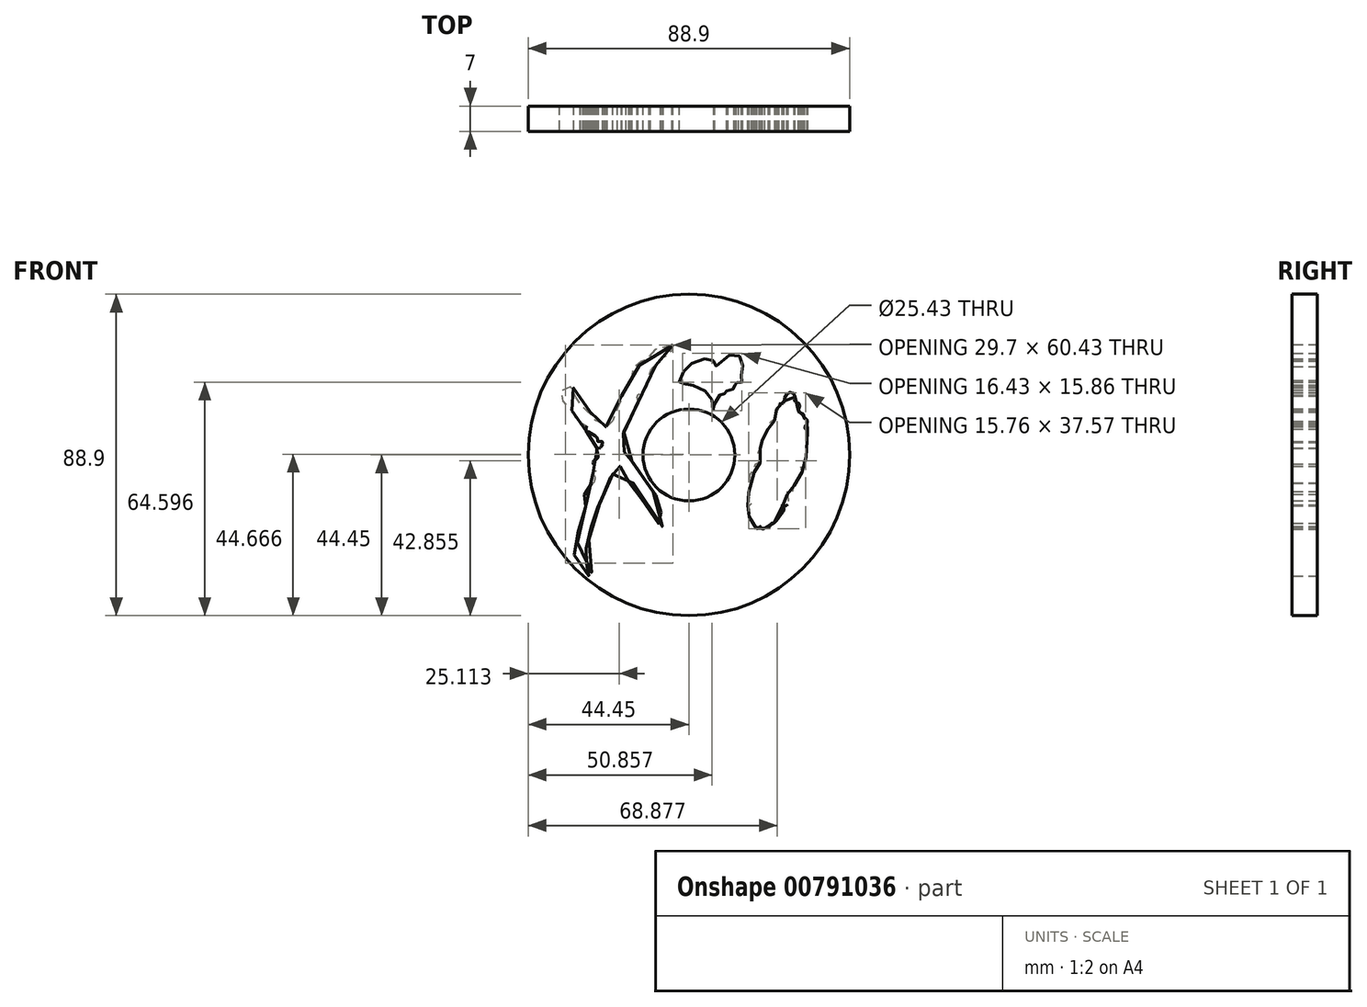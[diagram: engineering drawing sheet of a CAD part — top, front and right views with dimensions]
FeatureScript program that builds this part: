
annotation { "Feature Type Name" : "Feature", "Feature Type Description" : "" }
export const myFeature = defineFeature(function(context is Context, id is Id, definition is map)
    precondition{}
    {
        {
            var Q0;
            Q0=qCreatedBy(makeId("Front.planeOp"),FACE);
            var sketch = newSketch(context, id + "F0", { "sketchPlane" : qUnion([Q0])});
            skFitSpline(sketch, "E0", {"points": [v(-4.49, 30.43) * mm, v(-8.33, 29.49) * mm, v(-11.23, 27.84) * mm, v(-11.78, 26.27) * mm, v(-12.72, 26.04) * mm, v(-13.11, 26.27) * mm, v(-13.35, 25.25) * mm, v(-14.76, 24.16) * mm, v(-15.7, 23.53) * mm, v(-15.7, 22.12) * mm, v(-16.1, 20.78) * mm, v(-17.27, 20.24) * mm, v(-17.43, 18.51) * mm, v(-18.68, 16.08) * mm, v(-18.6, 14.98) * mm, v(-19.7, 13.57) * mm, v(-19.78, 12.32) * mm, v(-20.72, 10.98) * mm, v(-21.68, 7.22) * mm, v(-22.6, 7.7) * mm, v(-23.59, 7.83) * mm, v(-23.35, 8.76) * mm, v(-24.38, 8.53) * mm, v(-25.55, 8.44) * mm, v(-25.97, 9.65) * mm, v(-26.66, 10.26) * mm, v(-26.48, 10.82) * mm, v(-27.27, 11.23) * mm, v(-27.36, 11.89) * mm, v(-28.16, 11.89) * mm, v(-28.1, 12.45) * mm, v(-28.62, 13.61) * mm, v(-29.88, 13.8) * mm, v(-30.58, 14.78) * mm, v(-31.19, 15.8) * mm, v(-31.5, 18.08) * mm, v(-33.07, 18.86) * mm, v(-34.72, 18.63) * mm, v(-35.5, 17.3) * mm, v(-35.74, 15.8) * mm, v(-34.4, 14.4) * mm, v(-33.38, 13.3) * mm, v(-32.2, 12.04) * mm, v(-31.97, 11.1) * mm, v(-31.19, 10.16) * mm, v(-30.8, 9.3) * mm, v(-30.01, 9.3) * mm, v(-30.01, 8.43) * mm, v(-29.3, 8.43) * mm, v(-28.29, 8.12) * mm, v(-28.44, 6.79) * mm, v(-27.34, 6.16) * mm, v(-26.1, 5.37) * mm, v(-25.23, 4.51) * mm, v(-25.3, 3.73) * mm, v(-23.97, 3.73) * mm, v(-24.05, 2.7) * mm, v(-24.68, 1.85) * mm, v(-25.46, 1.85) * mm, v(-25.07, 0) * mm, v(-25.57, -1.23) * mm, v(-26.43, -1.7) * mm, v(-26.35, -2.95) * mm, v(-26.43, -3.97) * mm, v(-25.65, -4.52) * mm, v(-26.74, -4.75) * mm, v(-26.04, -5.85) * mm, v(-26.67, -7.9) * mm, v(-27.06, -7.66) * mm, v(-27.6, -8.6) * mm, v(-27.37, -9.77) * mm, v(-28.47, -10.24) * mm, v(-28.78, -12.12) * mm, v(-28.16, -12.6) * mm, v(-29.33, -13.3) * mm, v(-28.55, -14.09) * mm, v(-29.8, -15.5) * mm, v(-30.27, -17.3) * mm, v(-30.7, -21.9) * mm, v(-31.1, -25.2) * mm, v(-31.76, -26.38) * mm, v(-31.36, -29.15) * mm, v(-30.06, -31.39) * mm, v(-27.63, -33.44) * mm, v(-26.8, -32.6) * mm, v(-28.2, -32.32) * mm, v(-28.56, -30.92) * mm, v(-28.2, -29.24) * mm, v(-28.66, -27.94) * mm, v(-28, -27.47) * mm, v(-28.38, -26.73) * mm, v(-27.63, -23.37) * mm, v(-26.88, -21.78) * mm, v(-27.16, -20.38) * mm, v(-26.42, -18.33) * mm, v(-26.7, -17.87) * mm, v(-25.3, -15.26) * mm, v(-25.3, -14.14) * mm, v(-24.55, -13.4) * mm, v(-24.37, -12) * mm, v(-23.8, -11.62) * mm, v(-23.43, -10.31) * mm, v(-22.6, -9) * mm, v(-22.97, -8.07) * mm, v(-21.66, -6.2) * mm, v(-21.1, -5.18) * mm, v(-21, -4.06) * mm, v(-20.17, -3.32) * mm, v(-18.96, -3.13) * mm, v(-18.12, -4.16) * mm, v(-16.44, -6.58) * mm, v(-16.63, -7.6) * mm, v(-15.13, -7.89) * mm, v(-14.2, -9) * mm, v(-13.36, -11.34) * mm, v(-11.5, -15.53) * mm, v(-9.17, -18.24) * mm, v(-7.12, -19.82) * mm, v(-7.49, -18.05) * mm, v(-7.58, -16.37) * mm, v(-7.95, -14.42) * mm, v(-8.05, -13.3) * mm, v(-8.51, -12.18) * mm, v(-9.35, -10.78) * mm, v(-11.03, -8.45) * mm, v(-10.66, -8.07) * mm, v(-11.5, -7.52) * mm, v(-12.8, -6.2) * mm, v(-13.74, -5) * mm, v(-14.9, -2.74) * mm, v(-15.82, -1.69) * mm, v(-16.08, -1.1) * mm, v(-16.61, -0.83) * mm, v(-16.74, 0) * mm, v(-18.2, 1.08) * mm, v(-18.52, 2.8) * mm, v(-18.59, 4.64) * mm, v(-18.13, 5.76) * mm, v(-17.73, 7.22) * mm, v(-17.07, 7.94) * mm, v(-16.68, 8.8) * mm, v(-16.03, 10.63) * mm, v(-16.03, 11.93) * mm, v(-14.82, 12.77) * mm, v(-14.45, 13.99) * mm, v(-14.08, 14.73) * mm, v(-14.36, 16.22) * mm, v(-13.24, 17.16) * mm, v(-11.84, 18.55) * mm, v(-11.46, 19.67) * mm, v(-10.35, 23.68) * mm, v(-8.95, 24.9) * mm, v(-8.57, 25.36) * mm, v(-7.83, 25.74) * mm, v(-7.83, 26.76) * mm, v(-5.78, 27.6) * mm, v(-5.35, 28.64) * mm, v(-4.52, 28.92) * mm, v(-4.63, 29.7) * mm, v(-4.49, 30.43) * mm]});
            skFitSpline(sketch, "E1", {"points": [v(18.66, -20.38) * mm, v(17.56, -19.28) * mm, v(18.27, -18.5) * mm, v(16.39, -16.77) * mm, v(17.01, -15.28) * mm, v(17.01, -14.1) * mm, v(16.23, -14.1) * mm, v(17.48, -13.17) * mm, v(16.78, -12.07) * mm, v(16.62, -9.56) * mm, v(17.01, -5.33) * mm, v(18.03, -4.78) * mm, v(17.72, -3.52) * mm, v(18.58, -2.5) * mm, v(19.36, -2.5) * mm, v(19.84, 0) * mm, v(18.83, 1.07) * mm, v(19.75, 1.86) * mm, v(19.48, 3.31) * mm, v(21, 3.44) * mm, v(20.34, 4.17) * mm, v(20.8, 4.96) * mm, v(21.2, 5.82) * mm, v(21.66, 6.67) * mm, v(21.86, 7.2) * mm, v(22.39, 7.93) * mm, v(22.06, 8.59) * mm, v(22.58, 9.18) * mm, v(23.84, 9.64) * mm, v(23.84, 10.5) * mm, v(24.3, 11.95) * mm, v(24.1, 12.6) * mm, v(24.96, 13) * mm, v(24.63, 14) * mm, v(26.14, 14.32) * mm, v(26.34, 15.64) * mm, v(28.1, 17.33) * mm, v(29.31, 16.22) * mm, v(29.2, 15) * mm, v(30.64, 14) * mm, v(30.3, 12) * mm, v(31.75, 11.23) * mm, v(31.75, 10.23) * mm, v(32.64, 9.79) * mm, v(32.42, 8.12) * mm, v(31.97, 7.35) * mm, v(32.64, 6.8) * mm, v(32.64, 3.02) * mm, v(32.53, 0) * mm, v(31.42, -2.08) * mm, v(30.75, -3.08) * mm, v(31.3, -4.96) * mm, v(30.42, -5.85) * mm, v(29.98, -6.85) * mm, v(28.98, -8.73) * mm, v(28.2, -10.84) * mm, v(27.2, -10.17) * mm, v(27.43, -12.06) * mm, v(26.89, -14.08) * mm, v(25.79, -13.85) * mm, v(26.26, -14.87) * mm, v(25.32, -16.67) * mm, v(23.36, -18.86) * mm, v(22.8, -18.86) * mm, v(22.57, -19.33) * mm, v(21.87, -20.2) * mm, v(21.16, -20.12) * mm, v(20.61, -20.51) * mm, v(19.9, -20.2) * mm, v(19.75, -19.73) * mm, v(18.66, -20.38) * mm]});
            skCircle(sketch, "E2", {"center": v(0, 0) * mm, "radius": 12.71 * mm});
            skCircle(sketch, "E3", {"center": v(0, 0) * mm, "radius": 44.45 * mm});
            skPoint(sketch, "E4.23.internal.orphan", {"position": v(0, 19.2) * mm});
            skFitSpline(sketch, "E5", {"points": [v(6.68, 12.21) * mm, v(7.14, 12.68) * mm, v(7.05, 14.64) * mm, v(8.64, 16.6) * mm, v(9.66, 16.32) * mm, v(9.85, 17.06) * mm, v(10.78, 17.16) * mm, v(10.4, 18) * mm, v(11.8, 18.55) * mm, v(12.46, 18) * mm, v(12.55, 19.2) * mm, v(13.76, 19.11) * mm, v(13.2, 20.05) * mm, v(13.4, 20.6) * mm, v(14.88, 20.05) * mm, v(14.51, 21.26) * mm, v(14.79, 23.68) * mm, v(14.7, 25.36) * mm, v(13.67, 27.7) * mm, v(11.15, 27.6) * mm, v(6.96, 24.43) * mm, v(6.77, 25.83) * mm, v(5.74, 26.48) * mm, v(3.04, 26.3) * mm, v(-0.78, 24.24) * mm, v(-2, 21.82) * mm, v(-2.65, 20.05) * mm, v(-1.9, 20.33) * mm, v(-1.06, 19.2) * mm, v(1.73, 19.2) * mm, v(5.1, 17.06) * mm, v(6.4, 14.92) * mm, v(6.68, 12.21) * mm]});
            skSolve(sketch);
        }
        {
            var Q0;
            Q0 = qSketchRegion(id + "F0", true);
            extrude(context, id + "F1", {"entities" : qUnion([Q0]), "depth" : 7 * mm, "offsetDistance" : 25.4 * mm});
        }
    });
